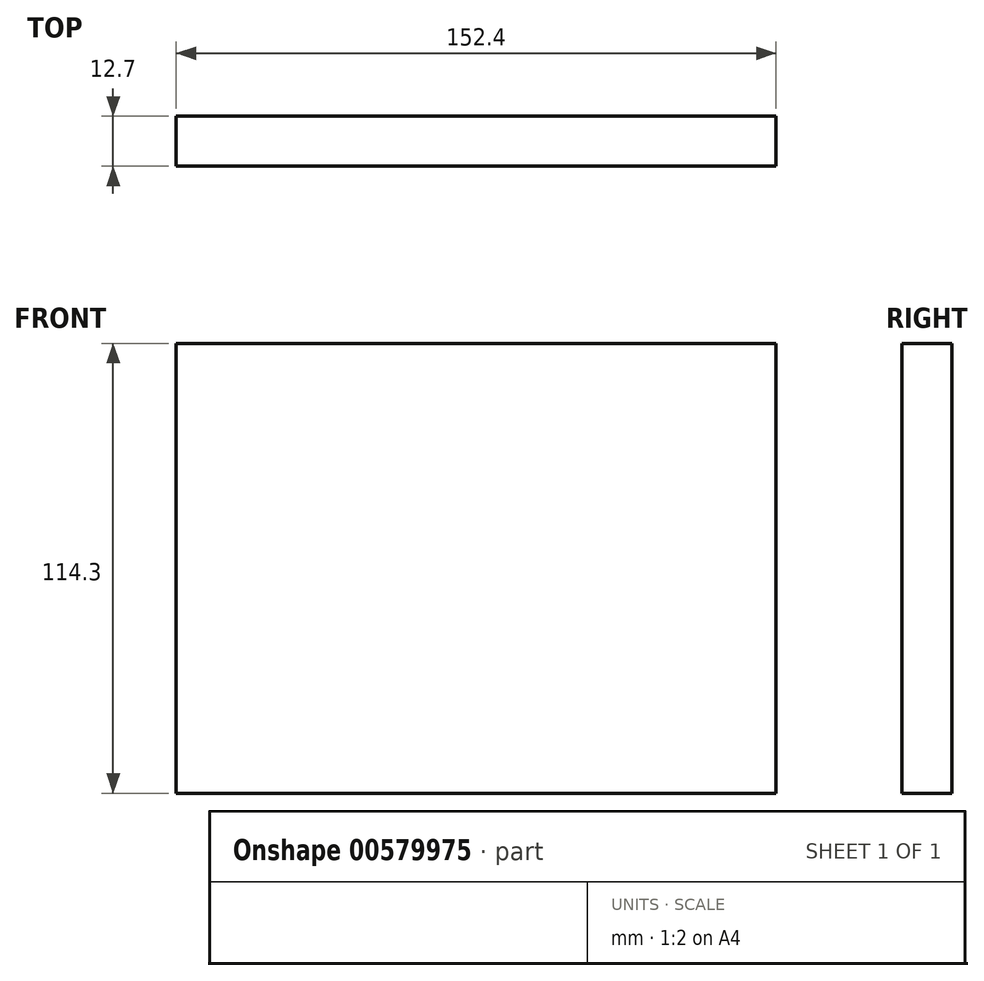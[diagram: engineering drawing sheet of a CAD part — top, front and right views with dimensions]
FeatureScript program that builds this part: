
annotation { "Feature Type Name" : "Feature", "Feature Type Description" : "" }
export const myFeature = defineFeature(function(context is Context, id is Id, definition is map)
    precondition{}
    {
        {
            var Q0;
            Q0=qCreatedBy(makeId("Front.planeOp"),FACE);
            var sketch = newSketch(context, id + "F0", { "sketchPlane" : qUnion([Q0])});
            skLineSegment(sketch, "E0", {"start": v(-74.17, 83.11) * mm, "end": v(-74.17, -31.19) * mm});
            skLineSegment(sketch, "E1", {"start": v(-74.17, -31.19) * mm, "end": v(78.23, -31.19) * mm});
            skLineSegment(sketch, "E2", {"start": v(78.23, -31.19) * mm, "end": v(78.23, 83.11) * mm});
            skLineSegment(sketch, "E3", {"start": v(78.23, 83.11) * mm, "end": v(-74.17, 83.11) * mm});
            skLineSegment(sketch, "E4", {"start": v(0, 83.11) * mm, "end": v(0, 0) * mm, "construction": true});
            skPoint(sketch, "E4.startSnap0", {"position": v(2.03, 83.11) * mm});
            skLineSegment(sketch, "E5", {"start": v(0, 0) * mm, "end": v(0, -31.19) * mm, "construction": true});
            skLineSegment(sketch, "E6", {"start": v(0, 0) * mm, "end": v(78.23, 0) * mm, "construction": true});
            skLineSegment(sketch, "E7", {"start": v(78.23, 0) * mm, "end": v(-74.17, 0) * mm, "construction": true});
            skSolve(sketch);
        }
        {
            var Q0;
            Q0=makeQuery(id+"F0.imprint","IMPRINT",FACE,{"disambiguationData":[TD([[makeQuery(id+"F0.imprint","IMPRINT",EDGE,{"derivedFrom":sQuery(id+"F0.wireOp",EDGE,"E0")}),1.0]])]});
            extrude(context, id + "F1", {"entities" : qUnion([Q0]), "depth" : 12.7 * mm, "offsetDistance" : 25.4 * mm});
        }
    });
